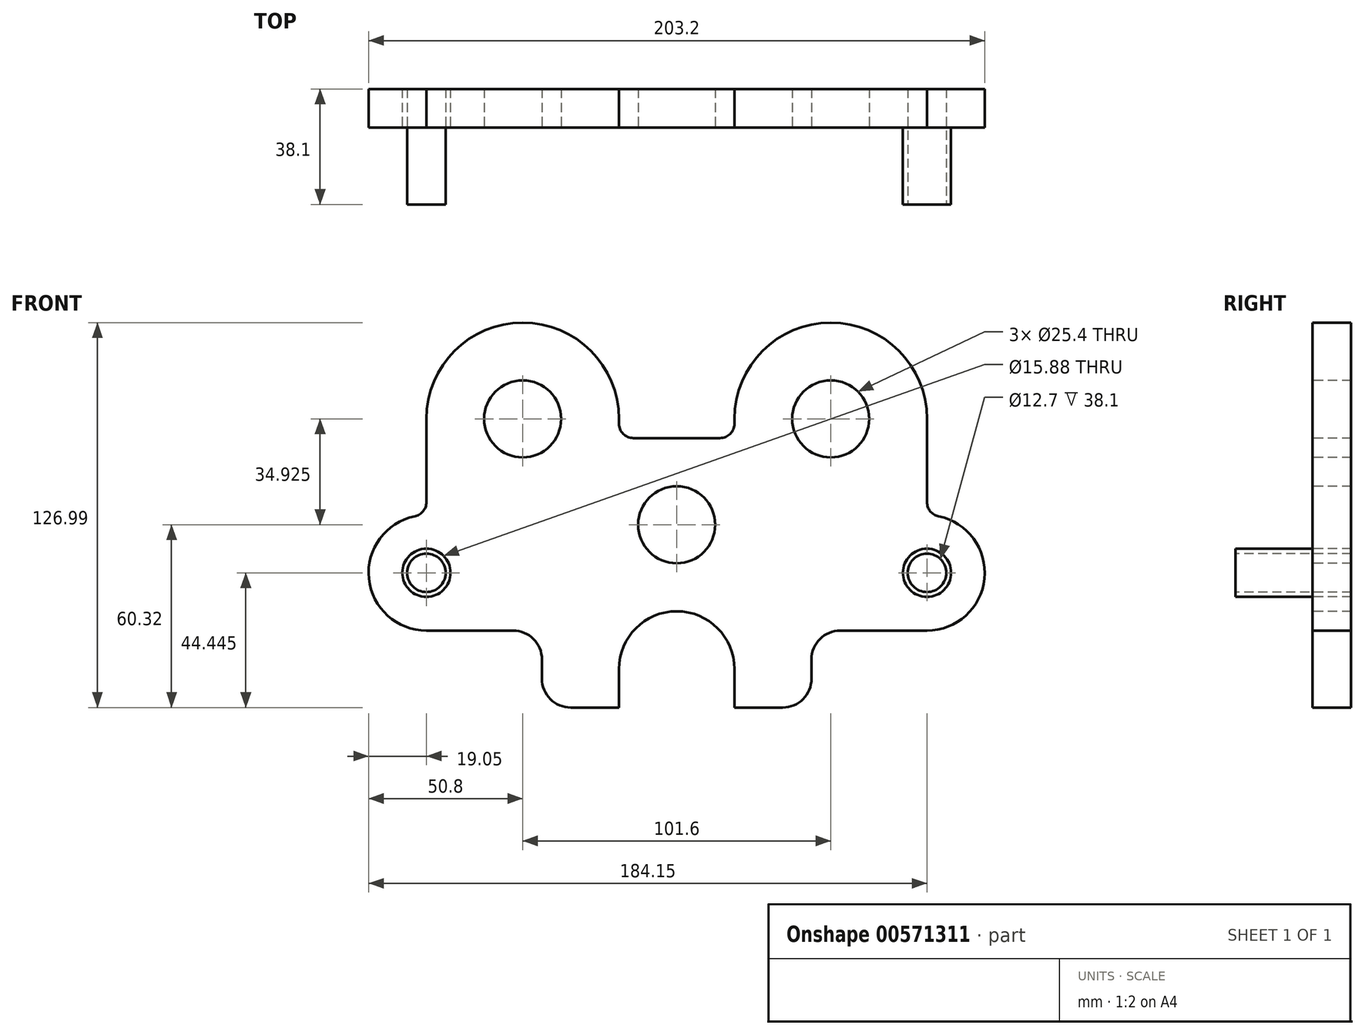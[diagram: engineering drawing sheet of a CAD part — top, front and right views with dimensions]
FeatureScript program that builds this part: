
annotation { "Feature Type Name" : "Feature", "Feature Type Description" : "" }
export const myFeature = defineFeature(function(context is Context, id is Id, definition is map)
    precondition{}
    {
        {
            var Q0;
            Q0=qCreatedBy(makeId("Front.planeOp"),FACE);
            var sketch = newSketch(context, id + "F0", { "sketchPlane" : qUnion([Q0])});
            skLineSegment(sketch, "E0", {"start": v(0, 76.7) * mm, "end": v(0, -75.9) * mm, "construction": true});
            skLineSegment(sketch, "E1", {"start": v(50.8, 76.08) * mm, "end": v(50.8, 12.52) * mm, "construction": true});
            skCircle(sketch, "E2", {"center": v(0, 0) * mm, "radius": 12.7 * mm});
            skCircle(sketch, "E3", {"center": v(50.8, 34.93) * mm, "radius": 12.7 * mm});
            skLineSegment(sketch, "E4", {"start": v(0, 28.58) * mm, "end": v(14.29, 28.58) * mm});
            skArc(sketch, "E5", {"start": v(82.55, 34.93) * mm, "mid": v(50.8, 66.68) * mm, "end": v(19.05, 34.93) * mm});
            skPoint(sketch, "E6.visualSharp", {"position": v(19.7, 28.58) * mm});
            skLineSegment(sketch, "E7", {"start": v(82.55, -34.92) * mm, "end": v(53.98, -34.92) * mm});
            skLineSegment(sketch, "E8", {"start": v(-29.42, 0) * mm, "end": v(25.25, 0) * mm, "construction": true});
            skCircle(sketch, "E9", {"center": v(82.55, -15.87) * mm, "radius": 6.35 * mm});
            skLineSegment(sketch, "E10", {"start": v(19.05, 34.93) * mm, "end": v(19.05, 33.34) * mm});
            skLineSegment(sketch, "E11", {"start": v(82.55, -7.94) * mm, "end": v(82.55, -31.6) * mm, "construction": true});
            skLineSegment(sketch, "E12", {"start": v(82.55, 34.93) * mm, "end": v(82.55, 7.46) * mm});
            skLineSegment(sketch, "E13", {"start": v(22.13, 34.93) * mm, "end": v(67.82, 34.93) * mm, "construction": true});
            skLineSegment(sketch, "E14", {"start": v(59.23, -15.87) * mm, "end": v(95.93, -15.87) * mm, "construction": true});
            skLineSegment(sketch, "E15", {"start": v(44.45, -44.45) * mm, "end": v(44.45, -50.8) * mm});
            skLineSegment(sketch, "E16", {"start": v(34.93, -60.32) * mm, "end": v(19.05, -60.32) * mm});
            skLineSegment(sketch, "E17", {"start": v(19.05, -60.32) * mm, "end": v(19.05, -47.62) * mm});
            skLineSegment(sketch, "E18.MirrorCS", {"start": v(0, 28.58) * mm, "end": v(-14.29, 28.58) * mm});
            skLineSegment(sketch, "E19.MirrorCS", {"start": v(-19.05, 34.93) * mm, "end": v(-19.05, 33.34) * mm});
            skArc(sketch, "E20.MirrorCS", {"start": v(-82.55, 34.93) * mm, "mid": v(-50.8, 66.68) * mm, "end": v(-19.05, 34.93) * mm});
            skLineSegment(sketch, "E21.MirrorCS", {"start": v(-82.55, 34.93) * mm, "end": v(-82.55, 7.46) * mm});
            skArc(sketch, "E22.MirrorCS", {"start": v(-82.55, -34.93) * mm, "mid": v(-101.5, -17.79) * mm, "end": v(-86.36, 2.8) * mm});
            skLineSegment(sketch, "E23.MirrorCS", {"start": v(-82.55, -34.93) * mm, "end": v(-53.97, -34.93) * mm});
            skLineSegment(sketch, "E24.MirrorCS", {"start": v(-44.45, -44.45) * mm, "end": v(-44.45, -50.8) * mm});
            skLineSegment(sketch, "E25.MirrorCS", {"start": v(-34.92, -60.32) * mm, "end": v(-19.05, -60.32) * mm});
            skLineSegment(sketch, "E26.MirrorCS", {"start": v(-19.05, -60.32) * mm, "end": v(-19.05, -47.62) * mm});
            skCircle(sketch, "E27.MirrorC", {"center": v(-50.8, 34.93) * mm, "radius": 12.7 * mm});
            skCircle(sketch, "E28.MirrorC", {"center": v(-82.55, -15.88) * mm, "radius": 6.35 * mm});
            skLineSegment(sketch, "E29.MirrorCS", {"start": v(-59.23, -15.87) * mm, "end": v(-95.93, -15.87) * mm, "construction": true});
            skLineSegment(sketch, "E30.MirrorCS", {"start": v(-82.55, -7.94) * mm, "end": v(-82.55, -31.6) * mm, "construction": true});
            skLineSegment(sketch, "E31.MirrorCS", {"start": v(-50.8, 76.08) * mm, "end": v(-50.8, 12.52) * mm, "construction": true});
            skLineSegment(sketch, "E32.MirrorCS", {"start": v(-22.13, 34.93) * mm, "end": v(-67.82, 34.93) * mm, "construction": true});
            skArc(sketch, "E33", {"start": v(19.05, -47.62) * mm, "mid": v(0, -28.57) * mm, "end": v(-19.05, -47.62) * mm});
            skPoint(sketch, "E34.visualSharp", {"position": v(-44.45, -34.92) * mm});
            skArc(sketch, "E34.filletArc", {"start": v(-44.45, -44.45) * mm, "mid": v(-47.24, -37.71) * mm, "end": v(-53.97, -34.93) * mm});
            skPoint(sketch, "E35.visualSharp", {"position": v(44.45, -34.92) * mm});
            skArc(sketch, "E35.filletArc", {"start": v(53.98, -34.92) * mm, "mid": v(47.24, -37.71) * mm, "end": v(44.45, -44.45) * mm});
            skPoint(sketch, "E36.visualSharp", {"position": v(44.45, -60.32) * mm});
            skArc(sketch, "E36.filletArc", {"start": v(34.93, -60.32) * mm, "mid": v(41.66, -57.54) * mm, "end": v(44.45, -50.8) * mm});
            skPoint(sketch, "E37.visualSharp", {"position": v(-44.45, -60.32) * mm});
            skArc(sketch, "E37.filletArc", {"start": v(-44.45, -50.8) * mm, "mid": v(-41.66, -57.54) * mm, "end": v(-34.92, -60.32) * mm});
            skLineSegment(sketch, "E38", {"start": v(0, -47.62) * mm, "end": v(26.3, -47.62) * mm, "construction": true});
            skLineSegment(sketch, "E39", {"start": v(26.3, -47.62) * mm, "end": v(-26.62, -47.62) * mm, "construction": true});
            skPoint(sketch, "E40.visualSharp", {"position": v(-82.55, 3.17) * mm});
            skArc(sketch, "E40.filletArc", {"start": v(-86.36, 2.8) * mm, "mid": v(-83.62, 4.44) * mm, "end": v(-82.55, 7.46) * mm});
            skArc(sketch, "E41.MirrorCS", {"start": v(82.55, -34.92) * mm, "mid": v(101.5, -17.79) * mm, "end": v(86.36, 2.8) * mm});
            skPoint(sketch, "E42.MirrorP", {"position": v(82.55, 3.18) * mm});
            skArc(sketch, "E43.MirrorCS", {"start": v(86.36, 2.8) * mm, "mid": v(83.62, 4.44) * mm, "end": v(82.55, 7.46) * mm});
            skPoint(sketch, "E44.visualSharp", {"position": v(-19.05, 28.57) * mm});
            skArc(sketch, "E44.filletArc", {"start": v(-19.05, 33.34) * mm, "mid": v(-17.66, 29.97) * mm, "end": v(-14.29, 28.58) * mm});
            skPoint(sketch, "E45.visualSharp", {"position": v(19.05, 28.58) * mm});
            skArc(sketch, "E45.filletArc", {"start": v(14.29, 28.58) * mm, "mid": v(17.66, 29.97) * mm, "end": v(19.05, 33.34) * mm});
            skCircle(sketch, "E46", {"center": v(82.55, -15.87) * mm, "radius": 7.94 * mm});
            skCircle(sketch, "E47", {"center": v(-82.55, -15.88) * mm, "radius": 7.94 * mm});
            skSolve(sketch);
        }
        {
            var Q0;
            Q0 = qSketchRegion(id + "F0", true);
            var Q1;
            Q1=makeQuery(id+"F0.imprint","IMPRINT",FACE,{"disambiguationData":[TD([[makeQuery(id+"F0.imprint","IMPRINT",EDGE,{"derivedFrom":sQuery(id+"F0.wireOp",EDGE,"E9")}),-1.0]])]});
            var Q2;
            Q2=makeQuery(id+"F0.imprint","IMPRINT",FACE,{"disambiguationData":[TD([[makeQuery(id+"F0.imprint","IMPRINT",EDGE,{"derivedFrom":sQuery(id+"F0.wireOp",EDGE,"E28.MirrorC")}),1.0]])]});
            extrude(context, id + "F1", {"entities" : qUnion([Q0, Q1, Q2]), "oppositeDirection" : true, "depth" : 12.7 * mm, "offsetDistance" : 25.4 * mm});
        }
        {
            var Q0;
            Q0=makeQuery(id+"F0.imprint","IMPRINT",FACE,{"disambiguationData":[TD([[makeQuery(id+"F0.imprint","IMPRINT",EDGE,{"derivedFrom":sQuery(id+"F0.wireOp",EDGE,"E28.MirrorC")}),1.0]])]});
            var Q1;
            Q1=makeQuery(id+"F0.imprint","IMPRINT",FACE,{"disambiguationData":[TD([[makeQuery(id+"F0.imprint","IMPRINT",EDGE,{"derivedFrom":sQuery(id+"F0.wireOp",EDGE,"E9")}),-1.0]])]});
            extrude(context, id + "F2", {"entities" : qUnion([Q0, Q1]), "operationType" : NewBodyOperationType.ADD, "depth" : 25.4 * mm, "offsetDistance" : 25.4 * mm});
        }
    });
